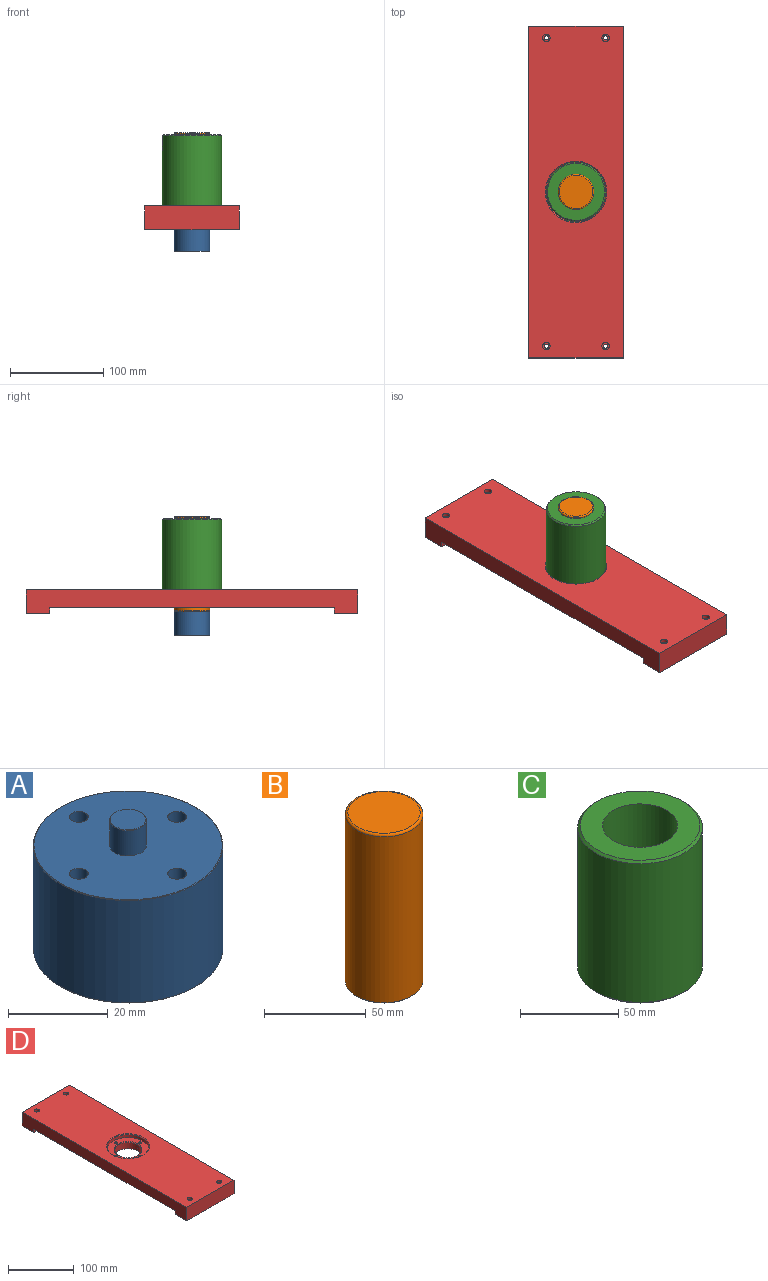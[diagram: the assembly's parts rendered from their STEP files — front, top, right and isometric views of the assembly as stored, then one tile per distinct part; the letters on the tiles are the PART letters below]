
ASSEMBLY  parts=4 mates=4
PART A: 23 faces, bbox 38.1x38.1x31.8 mm
  f0: cylinder r=19.05mm len=38.1mm, axis (0,0,-1), area 3009.8mm2, adj f6,f7
  f1: plane 37.85x37.85mm, normal (0,0,1), area 1037mm2, adj f7,f8,f11,f14,f17,f20
  f2: plane 37.85x37.85mm, normal (0,0,-1), area 760.3mm2, adj f5,f6,f13,f16,f19,f22
  f3: cylinder r=7.94mm len=15.88mm, axis (0,0,-1), area 152mm2, adj f4,f5
  f4: plane 15.88x15.88mm, normal (0,0,-1), area 197.9mm2, adj f3
  f5: cone r=8.06mm half-angle=45deg, axis (0,0,-1), area 9mm2, adj f2,f3
  f6: cone r=19.05mm half-angle=45deg, axis (0,0,1), area 21.4mm2, adj f0,f2
  f7: cone r=18.92mm half-angle=45deg, axis (0,0,-1), area 21.4mm2, adj f0,f1
  f8: cylinder r=3.68mm len=7.37mm, axis (0,0,-1), area 144mm2, adj f1,f10
  f9: plane 7.11x7.11mm, normal (0,0,1), area 39.7mm2, adj f10
  f10: cone r=3.56mm half-angle=45deg, axis (0,0,-1), area 4.1mm2, adj f8,f9
  f11: cylinder r=1.9mm len=21.89mm, axis (0,0,-1), area 261.2mm2, adj f1,f12
  f12: plane 7.14x7.14mm, normal (0,0,-1), area 28.8mm2, adj f11,f13
  f13: cylinder r=3.57mm len=7.14mm, axis (0,0,-1), area 78.7mm2, adj f2,f12
  f14: cylinder r=1.9mm len=21.89mm, axis (0,0,-1), area 261.2mm2, adj f1,f15
  f15: plane 7.14x7.14mm, normal (0,0,-1), area 28.8mm2, adj f14,f16
  f16: cylinder r=3.57mm len=7.14mm, axis (0,0,-1), area 78.7mm2, adj f2,f15
  f17: cylinder r=1.9mm len=21.89mm, axis (0,0,-1), area 261.2mm2, adj f1,f18
  f18: plane 7.14x7.14mm, normal (0,0,-1), area 28.8mm2, adj f17,f19
  f19: cylinder r=3.57mm len=7.14mm, axis (0,0,-1), area 78.7mm2, adj f2,f18
  f20: cylinder r=1.9mm len=21.89mm, axis (0,0,-1), area 261.2mm2, adj f1,f21
  f21: plane 7.14x7.14mm, normal (0,0,-1), area 28.8mm2, adj f20,f22
  f22: cylinder r=3.57mm len=7.14mm, axis (0,0,-1), area 78.7mm2, adj f2,f21
PART B: 16 faces, bbox 41.2x41.2x101.6 mm
  f0: cylinder r=19.05mm len=99.7mm, axis (0,0,-1), area 11933mm2, adj f14,f15
  f1: plane 35.56x35.56mm, normal (0,0,1), area 993.1mm2, adj f15
  f2: plane 36.83x36.83mm, normal (0,0,-1), area 958.4mm2, adj f5,f7,f9,f11,f13,f14
  f3: cylinder r=3.81mm len=7.62mm, axis (0,0,-1), area 121.6mm2, adj f4,f5
  f4: plane 7.62x7.62mm, normal (0,0,-1), area 45.6mm2, adj f3
  f5: cone r=3.81mm half-angle=45deg, axis (0,0,-1), area 50.2mm2, adj f2,f3
  f6: cone r=0mm half-angle=59deg, axis (0,0,-1), area 7.5mm2, adj f7
  f7: cylinder r=1.44mm len=6.35mm, axis (0,0,-1), area 57.3mm2, adj f2,f6
  f8: cone r=0mm half-angle=59deg, axis (0,0,-1), area 7.5mm2, adj f9
  f9: cylinder r=1.44mm len=6.35mm, axis (0,0,-1), area 57.3mm2, adj f2,f8
  f10: cone r=0mm half-angle=59deg, axis (0,0,-1), area 7.5mm2, adj f11
  f11: cylinder r=1.44mm len=6.35mm, axis (0,0,-1), area 57.3mm2, adj f2,f10
  f12: cone r=0mm half-angle=59deg, axis (0,0,-1), area 7.5mm2, adj f13
  f13: cylinder r=1.44mm len=6.35mm, axis (0,0,-1), area 57.3mm2, adj f2,f12
  f14: cone r=19.05mm half-angle=45deg, axis (0,0,1), area 105.7mm2, adj f0,f2
  f15: torus R=17.78mm, axis (0,0,1), area 233mm2, adj f0,f1
PART C: 15 faces, bbox 63.5x63.5x88.9 mm
  f0: cylinder r=31.75mm len=86.36mm, axis (0,0,-1), area 17228.1mm2, adj f3,f4
  f1: plane 60.96x60.96mm, normal (0,0,1), area 1775.5mm2, adj f3,f5
  f2: plane 60.96x60.96mm, normal (0,0,-1), area 1580.7mm2, adj f4,f6,f8,f10,f12,f14
  f3: cone r=30.48mm half-angle=45deg, axis (0,0,-1), area 351.1mm2, adj f0,f1
  f4: cone r=31.75mm half-angle=45deg, axis (0,0,1), area 351.1mm2, adj f0,f2
  f5: cylinder r=19.08mm len=87.63mm, axis (0,0,-1), area 10502.8mm2, adj f1,f6
  f6: cone r=20.35mm half-angle=45deg, axis (0,0,-1), area 222.4mm2, adj f2,f5
  f7: cone r=0mm half-angle=59deg, axis (0,0,-1), area 10.9mm2, adj f8
  f8: cylinder r=1.73mm len=6.83mm, axis (0,0,-1), area 74.1mm2, adj f2,f7
  f9: cone r=0mm half-angle=59deg, axis (0,0,-1), area 10.9mm2, adj f10
  f10: cylinder r=1.73mm len=6.83mm, axis (0,0,-1), area 74.1mm2, adj f2,f9
  f11: cone r=0mm half-angle=59deg, axis (0,0,-1), area 10.9mm2, adj f12
  f12: cylinder r=1.73mm len=6.83mm, axis (0,0,-1), area 74.1mm2, adj f2,f11
  f13: cone r=0mm half-angle=59deg, axis (0,0,-1), area 10.9mm2, adj f14
  f14: cylinder r=1.73mm len=6.83mm, axis (0,0,-1), area 74.1mm2, adj f2,f13
PART D: 39 faces, bbox 101.6x355.6x25.4 mm
  f0: plane 101.6x25.4mm, normal (0,0,-1), area 2548.9mm2, adj f1,f2,f3,f8,f31,f34
  f1: plane 355.6x25.4mm, normal (1,0,0), area 7096.8mm2, adj f0,f3,f4,f5,f6,f7,f8,f9
  f2: plane 355.6x25.4mm, normal (-1,0,0), area 7096.8mm2, adj f0,f3,f4,f5,f6,f7,f8,f9
  f3: plane 101.6x25.4mm, normal (0,-1,0), area 2580.6mm2, adj f0,f1,f2,f5
  f4: plane 101.6x25.4mm, normal (0,1,0), area 2580.6mm2, adj f1,f2,f5,f6
  f5: plane 355.6x101.6mm, normal (0,0,1), area 32532mm2, adj f1,f2,f3,f4,f27,f30,f33,f36
  f6: plane 101.6x25.4mm, normal (0,0,-1), area 2548.9mm2, adj f1,f2,f4,f7,f25,f28
  f7: plane 101.6x6.35mm, normal (0,-1,0), area 645.2mm2, adj f1,f2,f6,f9
  f8: plane 101.6x6.35mm, normal (0,1,0), area 645.2mm2, adj f0,f1,f2,f9
  f9: plane 304.8x101.6mm, normal (0,0,-1), area 29472.6mm2, adj f1,f2,f7,f8,f12,f15,f18,f21
  f10: cylinder r=31.88mm len=63.75mm, axis (0,0,1), area 1068.3mm2, adj f11,f37
  f11: plane 63.75x63.75mm, normal (0,0,1), area 1698.7mm2, adj f10,f13,f16,f19,f22,f38
  f12: cylinder r=20.32mm len=40.64mm, axis (0,0,1), area 1491.7mm2, adj f9,f38
  f13: cylinder r=2.25mm len=8.53mm, axis (0,0,-1), area 120.5mm2, adj f11,f14
  f14: plane 7.94x7.94mm, normal (0,0,-1), area 33.6mm2, adj f13,f15
  f15: cylinder r=3.97mm len=7.94mm, axis (0,0,-1), area 103.9mm2, adj f9,f14
  f16: cylinder r=2.25mm len=8.53mm, axis (0,0,-1), area 120.5mm2, adj f11,f17
  f17: plane 7.94x7.94mm, normal (0,0,-1), area 33.6mm2, adj f16,f18
  f18: cylinder r=3.97mm len=7.94mm, axis (0,0,-1), area 103.9mm2, adj f9,f17
  f19: cylinder r=2.25mm len=8.53mm, axis (0,0,-1), area 120.5mm2, adj f11,f20
  f20: plane 7.94x7.94mm, normal (0,0,-1), area 33.6mm2, adj f19,f21
  f21: cylinder r=3.97mm len=7.94mm, axis (0,0,-1), area 103.9mm2, adj f9,f20
  f22: cylinder r=2.25mm len=8.53mm, axis (0,0,-1), area 120.5mm2, adj f11,f23
  f23: plane 7.94x7.94mm, normal (0,0,-1), area 33.6mm2, adj f22,f24
  f24: cylinder r=3.97mm len=7.94mm, axis (0,0,-1), area 103.9mm2, adj f9,f23
  f25: cylinder r=2.25mm len=21.23mm, axis (0,0,1), area 299.9mm2, adj f6,f26
  f26: plane 7.94x7.94mm, normal (0,0,1), area 33.6mm2, adj f25,f27
  f27: cylinder r=3.97mm len=7.94mm, axis (0,0,1), area 103.9mm2, adj f5,f26
  f28: cylinder r=2.25mm len=21.23mm, axis (0,0,1), area 299.9mm2, adj f6,f29
  f29: plane 7.94x7.94mm, normal (0,0,1), area 33.6mm2, adj f28,f30
  f30: cylinder r=3.97mm len=7.94mm, axis (0,0,1), area 103.9mm2, adj f5,f29
  f31: cylinder r=2.25mm len=21.23mm, axis (0,0,1), area 299.9mm2, adj f0,f32
  f32: plane 7.94x7.94mm, normal (0,0,1), area 33.6mm2, adj f31,f33
  f33: cylinder r=3.97mm len=7.94mm, axis (0,0,1), area 103.9mm2, adj f5,f32
  f34: cylinder r=2.25mm len=21.23mm, axis (0,0,1), area 299.9mm2, adj f0,f35
  f35: plane 7.94x7.94mm, normal (0,0,1), area 33.6mm2, adj f34,f36
  f36: cylinder r=3.97mm len=7.94mm, axis (0,0,1), area 103.9mm2, adj f5,f35
  f37: cone r=31.88mm half-angle=45deg, axis (0,0,1), area 292.4mm2, adj f5,f10
  f38: cone r=20.32mm half-angle=45deg, axis (0,0,1), area 188mm2, adj f11,f12
PLACE A t=(0,0,12.57)mm
PLACE B t=(0,0,37.97)mm
PLACE C t=(0,0,48.51)mm
PLACE D t=(0,0,35.81)mm fixed
MATE cylindrical D.f12 <-> C.f0  axis (0,0,1) through (0,0,48.01)mm
MATE planar A.f0 <-> B.f0  axis (0,0,1) through (0,0,37.97)mm
MATE cylindrical A.f0 <-> C.f5  axis (0,0,-1) through (0,0,37.85)mm
MATE cylindrical A.f0 <-> B.f3  axis (0,0,-1) through (0,0,37.85)mm
